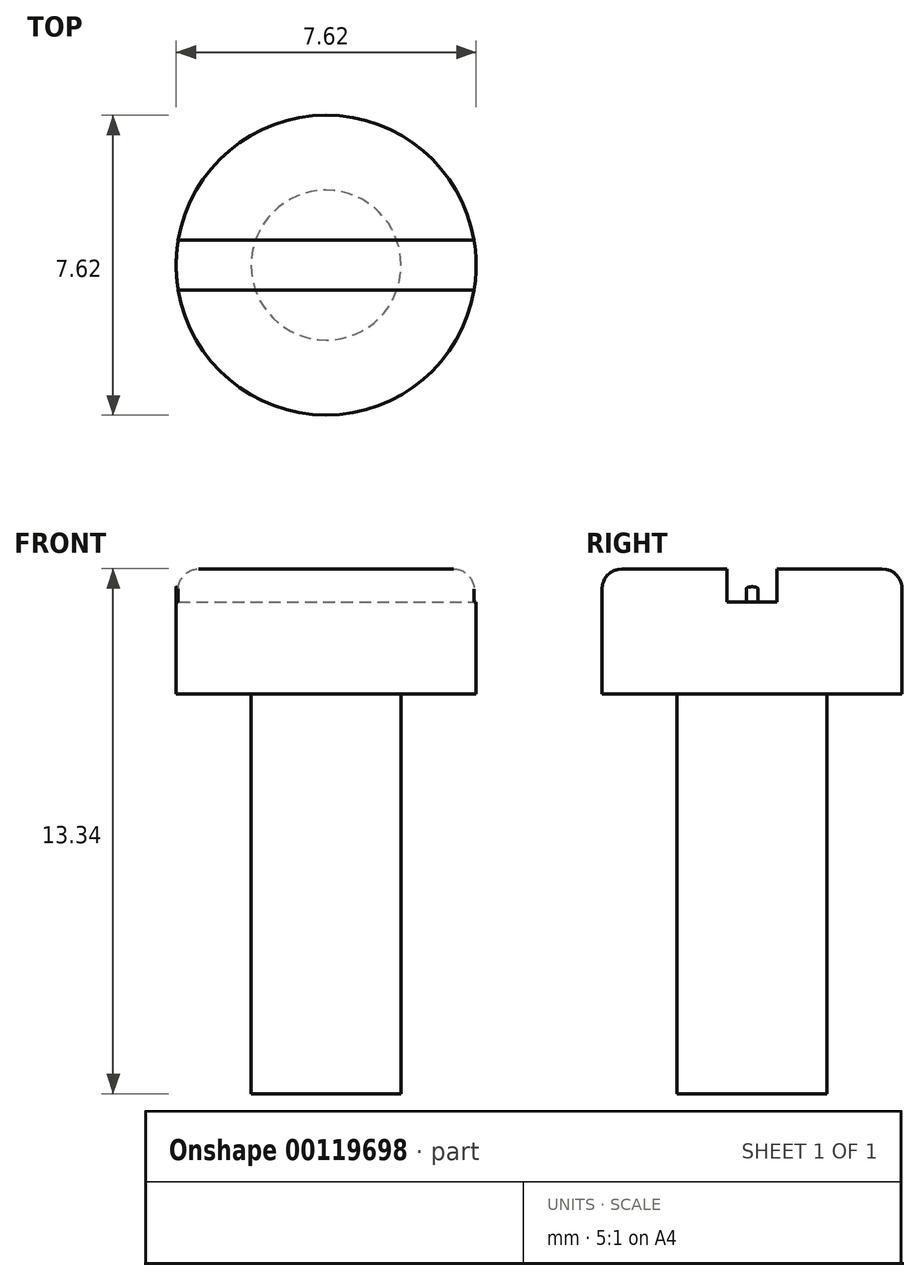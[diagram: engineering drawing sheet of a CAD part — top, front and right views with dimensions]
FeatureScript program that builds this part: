
annotation { "Feature Type Name" : "Feature", "Feature Type Description" : "" }
export const myFeature = defineFeature(function(context is Context, id is Id, definition is map)
    precondition{}
    {
        {
            var Q0;
            Q0=qCreatedBy(makeId("Front.planeOp"),FACE);
            var sketch = newSketch(context, id + "F0", { "sketchPlane" : qUnion([Q0])});
            skLineSegment(sketch, "E0.bottom", {"start": v(-3.8, 0) * mm, "end": v(3.81, 0) * mm});
            skLineSegment(sketch, "E0.top", {"start": v(-3.8, 3.18) * mm, "end": v(3.8, 3.18) * mm});
            skLineSegment(sketch, "E0.left", {"start": v(-3.8, 0) * mm, "end": v(-3.8, 3.18) * mm});
            skLineSegment(sketch, "E0.right", {"start": v(3.81, 0) * mm, "end": v(3.8, 3.18) * mm});
            skLineSegment(sketch, "E1.bottom", {"start": v(-1.9, 0) * mm, "end": v(1.9, 0) * mm});
            skLineSegment(sketch, "E1.right", {"start": v(1.9, 0) * mm, "end": v(1.9, -10.16) * mm});
            skLineSegment(sketch, "E2", {"start": v(0, -10.16) * mm, "end": v(0, 0) * mm});
            skLineSegment(sketch, "E3", {"start": v(1.9, -10.16) * mm, "end": v(0, -10.16) * mm});
            skSolve(sketch);
        }
        {
            var Q0;
            Q0=makeQuery(id+"F0.imprint","IMPRINT",FACE,{"disambiguationData":[TD([[makeQuery(id+"F0.imprint","IMPRINT",EDGE,{"derivedFrom":sQuery(id+"F0.wireOp",EDGE,"E0.top")}),-1.0]])]});
            extrude(context, id + "F1", {"entities" : qUnion([Q0]), "endBound" : BoundingType.SYMMETRIC, "depth" : 7.62 * mm});
        }
        {
            var Q0;
            Q0=makeQuery(id+"F1.opExtrude","CAP_EDGE",EDGE,{"disambiguationData":[OSD([sQuery(id+"F0.wireOp",EDGE,"E0.left")])],"isStart":false});
            var Q1;
            Q1=makeQuery(id+"F1.opExtrude","CAP_EDGE",EDGE,{"disambiguationData":[OSD([sQuery(id+"F0.wireOp",EDGE,"E0.left")])],"isStart":true});
            fillet(context, id + "F2", {"entities" : qUnion([Q0, Q1]), "radius" : 3.8 * mm, "tangentPropagation" : true, "allowEdgeOverflow" : false});
        }
        {
            var Q0;
            Q0=makeQuery(id+"F1.opExtrude","CAP_EDGE",EDGE,{"disambiguationData":[OSD([sQuery(id+"F0.wireOp",EDGE,"E0.right")])],"isStart":false});
            var Q1;
            Q1=makeQuery(id+"F1.opExtrude","CAP_EDGE",EDGE,{"disambiguationData":[OSD([sQuery(id+"F0.wireOp",EDGE,"E0.right")])],"isStart":true});
            fillet(context, id + "F3", {"entities" : qUnion([Q0, Q1]), "radius" : 3.8 * mm, "tangentPropagation" : true, "allowEdgeOverflow" : false});
        }
        {
            var Q0;
            {var subQ0=sQuery(id+"F0.wireOp",EDGE,"E1.right");Q0=makeQuery(id+"F0.imprint","IMPRINT",FACE,{"disambiguationData":[TD([[makeQuery(id+"F0.imprint","IMPRINT",EDGE,{"derivedFrom":subQ0}),-1.0]])]});}
            var Q1;
            Q1=sQuery(id+"F0.wireOp",EDGE,"E2");
            revolve(context, id + "F4", {"operationType" : NewBodyOperationType.ADD, "entities" : qUnion([Q0]), "axis" : qUnion([Q1]), "revolveType" : RevolveType.FULL});
        }
        {
            var Q0;
            Q0=makeQuery(id+"F2.opFillet","BLEND_EDGE",EDGE,{"blendedFrom":[makeQuery(id+"F1.opExtrude","CAP_EDGE",EDGE,{"disambiguationData":[OSD([sQuery(id+"F0.wireOp",EDGE,"E0.left")])],"isStart":false}),makeQuery(id+"F1.opExtrude","SWEPT_FACE",FACE,{"disambiguationData":[OSD([sQuery(id+"F0.wireOp",EDGE,"E0.top")])]})],"blendedInto":[makeQuery(id+"F1.opExtrude","SWEPT_FACE",FACE,{"disambiguationData":[OSD([sQuery(id+"F0.wireOp",EDGE,"E0.top")])]})]});
            var Q1;
            Q1=makeQuery(id+"F3.opFillet","BLEND_EDGE",EDGE,{"blendedFrom":[makeQuery(id+"F1.opExtrude","CAP_EDGE",EDGE,{"disambiguationData":[OSD([sQuery(id+"F0.wireOp",EDGE,"E0.right")])],"isStart":false}),makeQuery(id+"F1.opExtrude","SWEPT_FACE",FACE,{"disambiguationData":[OSD([sQuery(id+"F0.wireOp",EDGE,"E0.top")])]})],"blendedInto":[makeQuery(id+"F1.opExtrude","SWEPT_FACE",FACE,{"disambiguationData":[OSD([sQuery(id+"F0.wireOp",EDGE,"E0.top")])]})]});
            fillet(context, id + "F5", {"entities" : qUnion([Q0, Q1]), "radius" : 0.5 * mm, "tangentPropagation" : true, "allowEdgeOverflow" : false});
        }
        {
            var Q0;
            Q0=makeQuery(id+"F1.opExtrude","SWEPT_FACE",FACE,{"disambiguationData":[OSD([sQuery(id+"F0.wireOp",EDGE,"E0.top")])]});
            var sketch = newSketch(context, id + "F6", { "sketchPlane" : qUnion([Q0])});
            skLineSegment(sketch, "E4.bottom", {"start": v(-3.8, 0.63) * mm, "end": v(3.81, 0.64) * mm});
            skLineSegment(sketch, "E4.top", {"start": v(-3.8, -0.64) * mm, "end": v(3.81, -0.64) * mm});
            skLineSegment(sketch, "E4.left", {"start": v(-3.8, 0.63) * mm, "end": v(-3.8, -0.64) * mm});
            skLineSegment(sketch, "E4.right", {"start": v(3.81, 0.64) * mm, "end": v(3.81, -0.64) * mm});
            skSolve(sketch);
        }
        {
            var Q0;
            {var subQ0=sQuery(id+"F6.wireOp",EDGE,"E4.left");Q0=makeQuery(id+"F6.imprint","IMPRINT",FACE,{"disambiguationData":[TD([[makeQuery(id+"F6.imprint","IMPRINT",EDGE,{"derivedFrom":subQ0}),1.0]])]});}
            var Q1;
            {var subQ0=sQuery(id+"F6.wireOp",EDGE,"E4.bottom");var subQ1=makeQuery(id+"F1.opExtrude","SWEPT_FACE",FACE,{"disambiguationData":[OSD([sQuery(id+"F0.wireOp",EDGE,"E0.top")])]});var subQ2=makeQuery(id+"F5.opFillet","BLEND_EDGE",EDGE,{"blendedFrom":[makeQuery(id+"F2.opFillet","BLEND_EDGE",EDGE,{"blendedFrom":[makeQuery(id+"F1.opExtrude","CAP_EDGE",EDGE,{"disambiguationData":[OSD([sQuery(id+"F0.wireOp",EDGE,"E0.left")])],"isStart":false}),subQ1],"blendedInto":[subQ1]}),subQ1],"blendedInto":[subQ1]});var subQ3=makeQuery(id+"F6.imprint","INTERSECT",VERTEX,{"disambiguationData":[OD(0.0)],"derivedFrom":[subQ2,subQ0]});Q1=makeQuery(id+"F6.imprint","IMPRINT",FACE,{"disambiguationData":[TD([[makeQuery(id+"F6.imprint","IMPRINT",EDGE,{"disambiguationData":[TD([[subQ3,-1.0]])],"derivedFrom":subQ0}),-1.0]])]});}
            var Q2;
            {var subQ0=sQuery(id+"F6.wireOp",EDGE,"E4.right");Q2=makeQuery(id+"F6.imprint","IMPRINT",FACE,{"disambiguationData":[TD([[makeQuery(id+"F6.imprint","IMPRINT",EDGE,{"derivedFrom":subQ0}),-1.0]])]});}
            extrude(context, id + "F7", {"entities" : qUnion([Q0, Q1, Q2]), "operationType" : NewBodyOperationType.REMOVE, "oppositeDirection" : true, "depth" : 0.84 * mm});
        }
    });
